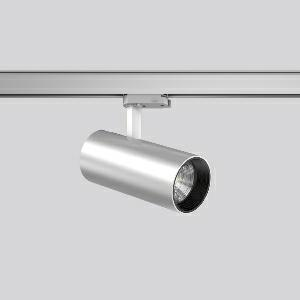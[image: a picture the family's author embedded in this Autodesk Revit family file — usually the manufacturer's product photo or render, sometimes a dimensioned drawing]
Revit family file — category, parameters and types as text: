
# Revit family: deecos_s_mini_742199_004_3_76_1bf3
name_source: partatom
category: Lighting Fixtures
units: mm (PartAtom-declared; Revit-internal decimal feet)

## family parameters
Cut with Voids When Loaded = No
Host = Face
Light Source = No
Part Type = Normal
Room Calculation Point = No
Round Connector Dimension = Use Diameter
Shared = No

## types (1)
- DEECOS S mini (1 x LED Modul 935, 2150 lm, 3500)
    Apparent Load = 20 VA
    Approval mark = CE
    CIE Flux Codes = 96 100 100 100 100
    Color Rendering = 92
    Color Temperature = 3500
    Default Elevation = 1800 mm
    Description = Series: DEECOS S mini
LED surface-mounted projector in modern design with no visible cooling ribs. Housing: die-cast aluminium, powder-coated. Rotation range: 356°. Swivel range: 90°. Black plastic ring and recessed LED to prevent glare from the side. Optical assembly with lens made of plastic (polycarbonate) for the best homogeneous light distribution - can be changed without tools. Best colour rendering index Ra>90. With adapter for RZB 3-circuit DALI tracks. Suitable for Track on ceiling, Wall track. High quality converter without flickering and stroboscopic effect. The following accessories can be mounted without use of tools: interchangeable lenses, decorative glasses, honeycomb louvre, clear and frosted diffusers, white interchangeable plastic ring. 
Colour: silver
Diameter: 87 mm
Height: 214 mm
Lamp: LED
Socket: without socket
Colour temperature: 3500K
Colour rendering index (CRI): 92
System power: 20 W
Rated luminous flux: 2150 lm
Luminous efficiency: 108 lm/W
Control gear: Converter, dimmable, DALI
Protection class: I
Type of protection: IP 20
    Height = 214 mm
    Lamp = 1 x LED Modul 935
    Lamp Light Flux = 2150 lm
    Lamp count = 1
    Length = 87 mm
    Lifetime = 50000 h
    Luminous efficacy = 108 lm/W
    Manufacturer = RZB
    ModVariant = No
    Model = 742199.004.3.76
    Mounting Place = Ceiling
    Mounting Type = Rail mounted
    Number of Poles = 1
    OnlyDefault = Yes
    Power Factor = 1
    Product Name = DEECOS S mini
    Product group = Track mounted projectors
    ProductGroupID = 301
    Protection Class = Protection class I
    Protection Degree = IP 20
    RLX_Detail_Level = 1
    RLX_Emergency_Light_Flux = 0 lm
    RLX_Emergency_Type = 0
    RLX_Emergency_Type_DB = No
    RlxData = <blob elided: 37385 chars, md5=3fc68c40>
    Socket = socket
    Standby Power = 0 W
    System Light Flux = 2150 lm
    System Power = 20 W
    Type Comments = Product without accessories
    Type Image = 741930.004.jpg
    URL = http://relux.com
    VarID = ---
    Voltage = 230 V
    Voltage Range = 220-240 V
    Weight = 0.00 kg
    Width = 0 mm  [stored 0 ft]

note: [stored X ft] marks values corroborated as IEEE doubles in the binary element streams (Revit-internal decimal feet)

## geometry (parser evidence)
native form markers: Blend x4, Sweep x13
no freeform markers — native parametric forms only
